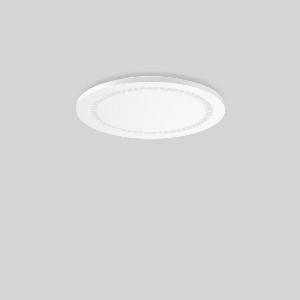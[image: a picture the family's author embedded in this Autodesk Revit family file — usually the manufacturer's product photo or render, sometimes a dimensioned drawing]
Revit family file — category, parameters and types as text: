
# Revit family: hemis_round_312186_002_2_98de
name_source: partatom
category: Lighting Fixtures
units: mm (PartAtom-declared; Revit-internal decimal feet)

## family parameters
Cut with Voids When Loaded = No
Host = Face
Light Source = No
Part Type = Normal
Room Calculation Point = No
Round Connector Dimension = Use Diameter
Shared = No

## types (1)
- MultiLumen 1 (1 x LED Modul 830, 3200 lm, 3000)
    Apparent Load = 25 VA
    CIE Flux Codes = 85 98 100 100 100
    Color Rendering = 80
    Color Temperature = 3000
    Default Elevation = 1800 mm
    Description = Series: HEMIS round
Glare-free LED ceiling luminaire with optical lens system. Base: metal, powder-coated, with bayonet fixing. Housing: plastic (polycarbonate). Housing and diffuser are screwed together. Diffuser with optic lenses. Big terminal block; ideal for through-wiring. Sealing strip on the back of the luminaire connects seamlessly with the ceiling. Easy installation with Plug+Play plug connection. Thanks to RUG < 22 ideal for corridors, stairways, shops, schools, meeting rooms, rest areas. 
Colour: white
Diameter: 400 mm
Height: 33 mm
Lamp: LED
Socket: without socket
Colour temperature: 3000K
Colour rendering index (CRI): 80
System power: 25 W
Rated luminous flux: 3200 lm
Luminous efficiency: 128 lm/W
System power 2: 22 W
Rated luminous flux 2: 2750 lm
Luminous efficiency 2: 125 lm/W
Control gear: Regulated power supply
Protection class: I
Type of protection: IP 40
    Height = 33 mm
    Lamp = 1 x LED Modul 830
    Lamp Light Flux = 3200 lm
    Lamp count = 1
    Length = 400 mm
    Lifetime = 50000 h
    Luminous efficacy = 128 lm/W
    Manufacturer = RZB
    ModVariant = No
    Model = 312186.002.2
    Mounting Place = Ceiling
    Mounting Type = Surface mounted
    Number of Poles = 1
    OnlyDefault = Yes
    Power Factor = 1
    Product Name = HEMIS round
    Product group = Surface mounted modular luminaires
    ProductGroupID = 306
    Protection Class = Protection class I
    Protection Degree = Degree of protection
    RLX_Detail_Level = 1
    RLX_Emergency_Light_Flux = 0 lm
    RLX_Emergency_Type = 0
    RLX_Emergency_Type_DB = No
    RlxData = <blob elided: 41633 chars, md5=dd1b8332>
    Socket = socket
    Standby Power = 0 W
    System Light Flux = 3200 lm
    System Power = 25 W
    Type Comments = MultiLumen 1
    Type Image = 312186.002.jpg
    URL = http://relux.com
    VarID = multilumen_1
    Voltage = 0 V
    Weight = 0.00 kg
    Width = 0 mm  [stored 0 ft]

note: [stored X ft] marks values corroborated as IEEE doubles in the binary element streams (Revit-internal decimal feet)

## geometry (parser evidence)
native form markers: Blend x4, Sweep x10
no freeform markers — native parametric forms only
